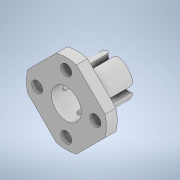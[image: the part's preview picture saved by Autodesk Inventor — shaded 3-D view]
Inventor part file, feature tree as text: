
AUTODESK INVENTOR PART (.ipt)
format: ipt  version: 2020 (Build 240168000, 168)  size: 239,104 bytes
history: native  units: in
note: dims shown in document units (in); Inventor stores cm internally (conversion verified against a paired STEP export)
features: reference x6, extrude x5, sketch x5, other x4, fillet x2, projected_geometry x2
ambient origin geometry x8: Origin, YZ Plane, XZ Plane, XY Plane, X Axis, Y Axis, Z Axis, Center Point
bodies: Solid1 (feature_tree)
feature tree (24):
  extrude  "Extrusion1"  Depth=0.4331in
  extrude  "Extrusion2"  Depth=0.3937in
  extrude  "Extrusion3"  Depth=0.1181in TaperAngle=0.0deg
  extrude  "Extrusion4"  Depth=1.1811in
  fillet  "Fillet1"  Radius=1.1811in
  fillet  "Fillet2"  Radius=0.0591in
  extrude  "Extrusion5"  Depth=0.0394in
  sketch  "Sketch1"  dims[d0=0.3228in d1=0.4331in]
  reference  "Reference1"
  reference  "Reference2"
  sketch  "Sketch2"  dims[d2=0.3937in d3=0.0in d4=0.8661in]
  sketch  "Sketch3"  dims[d5=0.1181in d6=0.0in d7=0.1575in d8=0.0in]
  reference  "Reference3"
  reference  "Reference4"
  reference  "Reference5"
  reference  "Reference6"
  sketch  "Sketch4"  dims[d9=0.0591in d10=1.1811in d11=1.1811in d12=0.0591in]
  projected_geometry  "Projected Loop1"
  sketch  "Sketch5"  dims[d13=0.3937in d14=0.0in d15=0.0394in d16=0.0394in d17=0.748in d18=135.0deg d19=0.748in d20=0.3937in d21=0.0in]
  projected_geometry  "Projected Loop2"
  parser-record x1  (decoder bookkeeping rows leaked as tree rows — omitted from the tree; the rows remain in map.json)
  other  "arm_shift_1.iam"
  other  "pin_8_45:1"
  other  "120teeth gt2 pulley:1"
note: 1 file-system path scrubbed to <path> (originals preserved in map.json)
